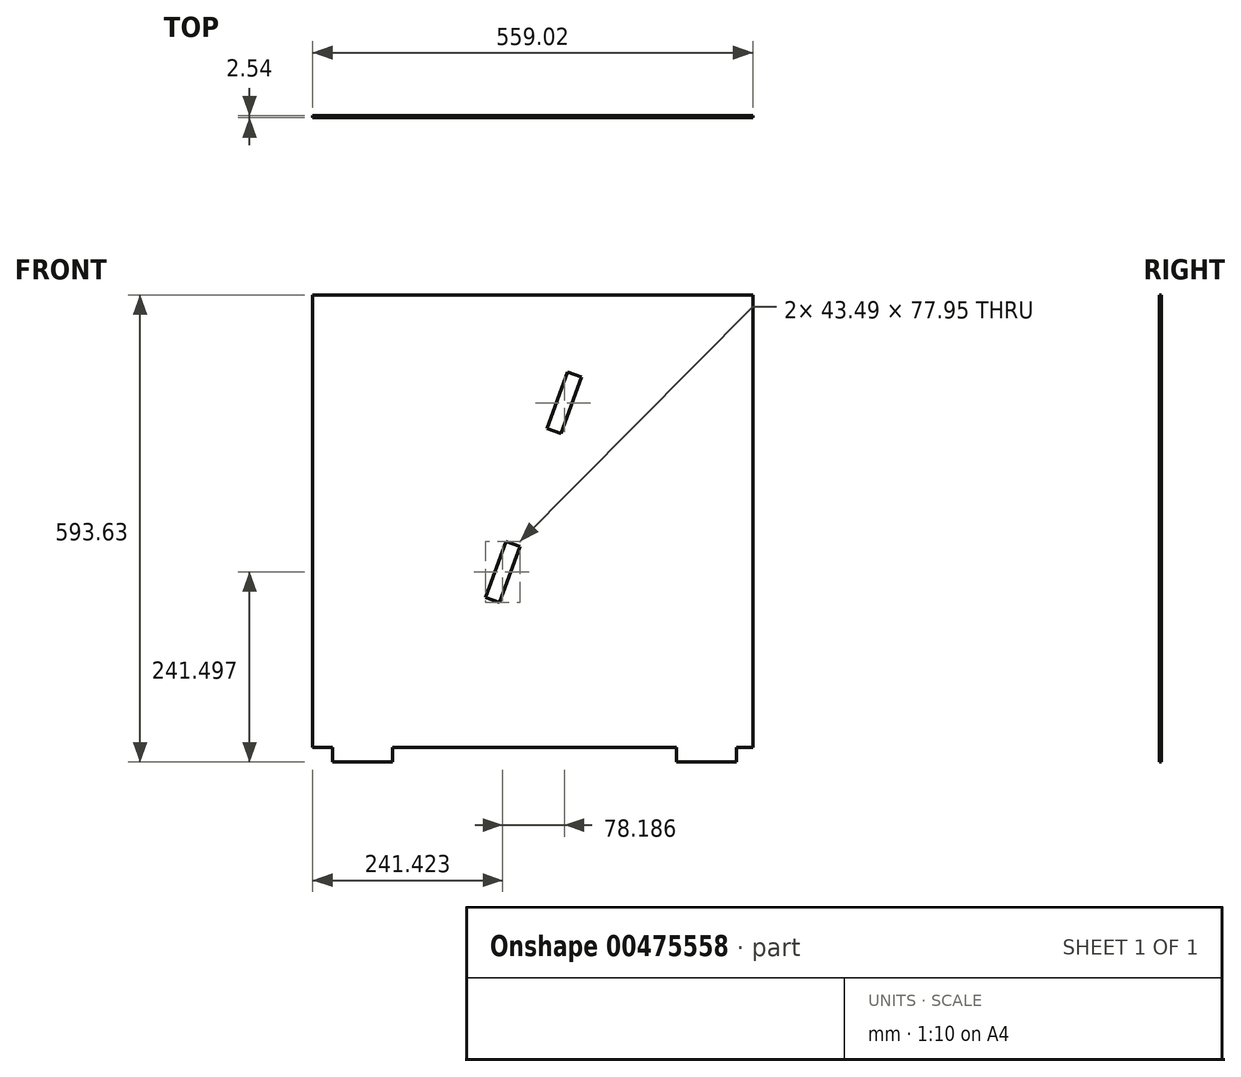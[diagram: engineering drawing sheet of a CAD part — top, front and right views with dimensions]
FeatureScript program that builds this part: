
annotation { "Feature Type Name" : "Feature", "Feature Type Description" : "" }
export const myFeature = defineFeature(function(context is Context, id is Id, definition is map)
    precondition{}
    {
        {
            var Q0;
            Q0=qCreatedBy(makeId("Front.planeOp"),FACE);
            var sketch = newSketch(context, id + "F0", { "sketchPlane" : qUnion([Q0])});
            skLineSegment(sketch, "E0.top", {"start": v(-219.68, -307.88) * mm, "end": v(-194.28, -307.88) * mm});
            skLineSegment(sketch, "E0.left", {"start": v(-219.68, 267.21) * mm, "end": v(-219.68, -307.88) * mm});
            skLineSegment(sketch, "E1", {"start": v(-194.28, -307.88) * mm, "end": v(-194.28, -326.42) * mm});
            skLineSegment(sketch, "E2", {"start": v(-194.28, -326.42) * mm, "end": v(-118.08, -326.42) * mm});
            skLineSegment(sketch, "E3", {"start": v(-118.08, -326.42) * mm, "end": v(-118.08, -307.88) * mm});
            skLineSegment(sketch, "E4", {"start": v(-118.08, -307.88) * mm, "end": v(242.55, -307.88) * mm});
            skLineSegment(sketch, "E5", {"start": v(242.55, -307.88) * mm, "end": v(242.55, -326.42) * mm});
            skLineSegment(sketch, "E6", {"start": v(242.55, -326.42) * mm, "end": v(318.75, -326.42) * mm});
            skLineSegment(sketch, "E7", {"start": v(318.75, -326.42) * mm, "end": v(318.75, -307.88) * mm});
            skLineSegment(sketch, "E8", {"start": v(318.75, -307.88) * mm, "end": v(339.34, -307.88) * mm});
            skLineSegment(sketch, "E9.bottom", {"start": v(26.06, -45.95) * mm, "end": v(43.49, -52.3) * mm});
            skLineSegment(sketch, "E9.top", {"start": v(0, -117.55) * mm, "end": v(17.42, -123.9) * mm});
            skLineSegment(sketch, "E9.left", {"start": v(26.06, -45.95) * mm, "end": v(0, -117.55) * mm});
            skLineSegment(sketch, "E9.right", {"start": v(43.49, -52.3) * mm, "end": v(17.42, -123.9) * mm});
            skLineSegment(sketch, "E10.bottom", {"start": v(78.19, 97.26) * mm, "end": v(95.6, 90.92) * mm});
            skLineSegment(sketch, "E10.top", {"start": v(104.25, 168.86) * mm, "end": v(121.67, 162.52) * mm});
            skLineSegment(sketch, "E10.left", {"start": v(78.19, 97.26) * mm, "end": v(104.25, 168.86) * mm});
            skLineSegment(sketch, "E10.right", {"start": v(95.6, 90.92) * mm, "end": v(121.67, 162.52) * mm});
            skPoint(sketch, "E11.startSnap0", {"position": v(85.12, -307.88) * mm});
            skPoint(sketch, "E11.start.orphan", {"position": v(0, -307.88) * mm});
            skLineSegment(sketch, "E12", {"start": v(339.34, -307.88) * mm, "end": v(339.34, 267.21) * mm});
            skLineSegment(sketch, "E13", {"start": v(-219.68, 267.21) * mm, "end": v(339.34, 267.21) * mm});
            skSolve(sketch);
        }
        {
            var Q0;
            Q0=makeQuery(id+"F0.imprint","IMPRINT",FACE,{"disambiguationData":[TD([[makeQuery(id+"F0.imprint","IMPRINT",EDGE,{"derivedFrom":sQuery(id+"F0.wireOp",EDGE,"E0.left")}),1.0]])]});
            extrude(context, id + "F1", {"entities" : qUnion([Q0]), "depth" : 2.54 * mm, "offsetDistance" : 25.4 * mm});
        }
    });
